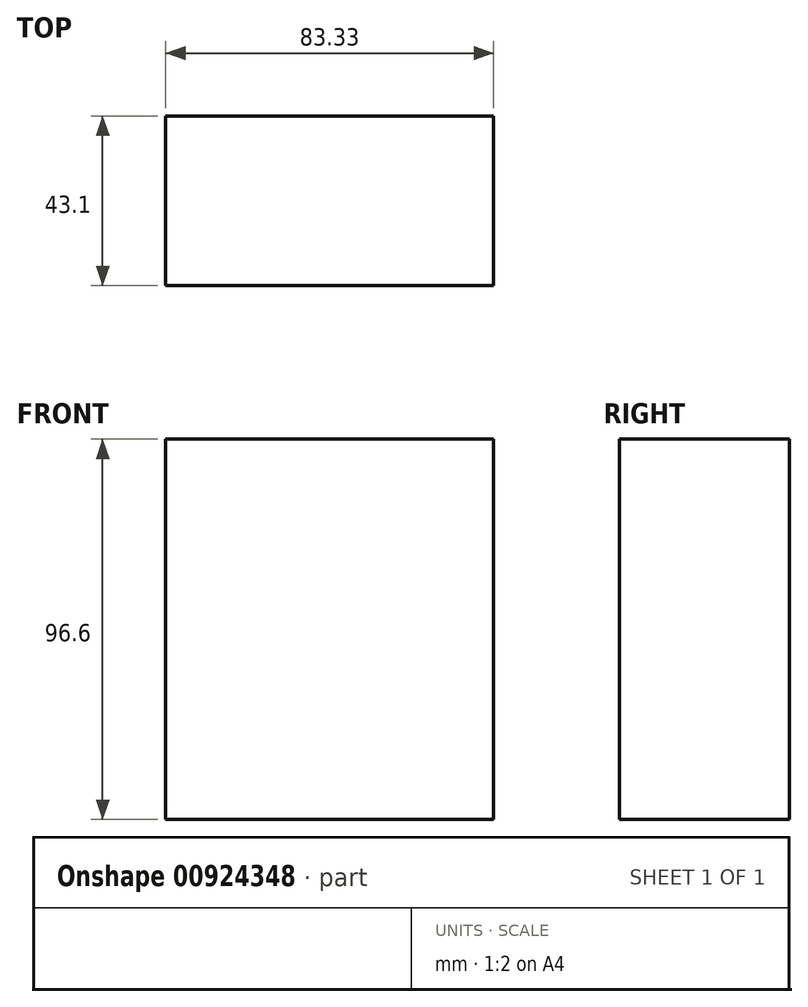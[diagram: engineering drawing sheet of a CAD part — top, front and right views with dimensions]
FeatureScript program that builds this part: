
annotation { "Feature Type Name" : "Feature", "Feature Type Description" : "" }
export const myFeature = defineFeature(function(context is Context, id is Id, definition is map)
    precondition{}
    {
        {
            var Q0;
            Q0=qCreatedBy(makeId("Right.planeOp"),FACE);
            var sketch = newSketch(context, id + "F0", { "sketchPlane" : qUnion([Q0])});
            skLineSegment(sketch, "E0.bottom", {"start": v(66.73, 86.68) * mm, "end": v(-66.73, 86.68) * mm});
            skLineSegment(sketch, "E0.top", {"start": v(66.73, -9.92) * mm, "end": v(-66.73, -9.92) * mm});
            skLineSegment(sketch, "E0.left", {"start": v(66.73, 86.68) * mm, "end": v(66.73, -9.92) * mm});
            skLineSegment(sketch, "E0.right", {"start": v(-66.73, 86.68) * mm, "end": v(-66.73, -9.92) * mm});
            skPoint(sketch, "E0.middle", {"position": v(0, 38.38) * mm});
            skLineSegment(sketch, "E1.bottom", {"start": v(66.73, 38.38) * mm, "end": v(-200.2, 38.38) * mm, "construction": true});
            skLineSegment(sketch, "E1.top", {"start": v(66.73, 38.38) * mm, "end": v(-200.2, 38.38) * mm, "construction": true});
            skLineSegment(sketch, "E1.left", {"start": v(66.73, 38.38) * mm, "end": v(66.73, 38.38) * mm});
            skLineSegment(sketch, "E1.right", {"start": v(-200.2, 38.38) * mm, "end": v(-200.2, 38.38) * mm});
            skPoint(sketch, "E1.middle", {"position": v(-66.73, 38.38) * mm});
            skLineSegment(sketch, "E2.bottom", {"start": v(-16.33, -9.92) * mm, "end": v(-117.13, -9.92) * mm, "construction": true});
            skLineSegment(sketch, "E2.top", {"start": v(-16.33, 133.1) * mm, "end": v(-117.13, 133.1) * mm, "construction": true});
            skLineSegment(sketch, "E2.left", {"start": v(-16.33, -9.92) * mm, "end": v(-16.33, 133.1) * mm, "construction": true});
            skLineSegment(sketch, "E2.right", {"start": v(-117.13, -9.92) * mm, "end": v(-117.13, 133.1) * mm, "construction": true});
            skPoint(sketch, "E2.middle", {"position": v(-66.73, 61.6) * mm});
            skLineSegment(sketch, "E3.bottom", {"start": v(66.73, -42.53) * mm, "end": v(66.73, -42.53) * mm});
            skLineSegment(sketch, "E3.top", {"start": v(66.73, 22.69) * mm, "end": v(66.73, 22.69) * mm});
            skLineSegment(sketch, "E3.left", {"start": v(66.73, -42.53) * mm, "end": v(66.73, 22.69) * mm, "construction": true});
            skLineSegment(sketch, "E3.right", {"start": v(66.73, -42.53) * mm, "end": v(66.73, 22.69) * mm, "construction": true});
            skPoint(sketch, "E3.middle", {"position": v(66.73, -9.92) * mm});
            skLineSegment(sketch, "E4.bottom", {"start": v(23.63, 86.68) * mm, "end": v(-157.1, 86.68) * mm});
            skLineSegment(sketch, "E4.top", {"start": v(23.63, -106.52) * mm, "end": v(-157.1, -106.52) * mm});
            skLineSegment(sketch, "E4.left", {"start": v(23.63, 86.68) * mm, "end": v(23.63, -106.52) * mm});
            skLineSegment(sketch, "E4.right", {"start": v(-157.1, 86.68) * mm, "end": v(-157.1, -106.52) * mm});
            skPoint(sketch, "E4.middle", {"position": v(-66.73, -9.92) * mm});
            skSolve(sketch);
        }
        {
            var Q0;
            {var subQ0=sQuery(id+"F0.wireOp",EDGE,"E0.bottom");Q0=makeQuery(id+"F0.imprint","IMPRINT",FACE,{"disambiguationData":[TD([[makeQuery(id+"F0.imprint","IMPRINT",EDGE,{"derivedFrom":subQ0}),1.0]])]});}
            var sketch = newSketch(context, id + "F1", { "sketchPlane" : qUnion([Q0])});
            skSolve(sketch);
        }
        {
            var Q0;
            {var subQ0=sQuery(id+"F0.wireOp",EDGE,"E0.bottom");Q0=makeQuery(id+"F1.imprint","IMPRINT",FACE,{"disambiguationData":[TD([[makeQuery(id+"F1.imprint","IMPRINT",EDGE,{"derivedFrom":makeQuery(id+"F0.imprint","IMPRINT",EDGE,{"derivedFrom":subQ0})}),1.0]])]});}
            extrude(context, id + "F2", {"entities" : qUnion([Q0]), "depth" : 83.33 * mm, "offsetDistance" : 25.4 * mm});
        }
    });
